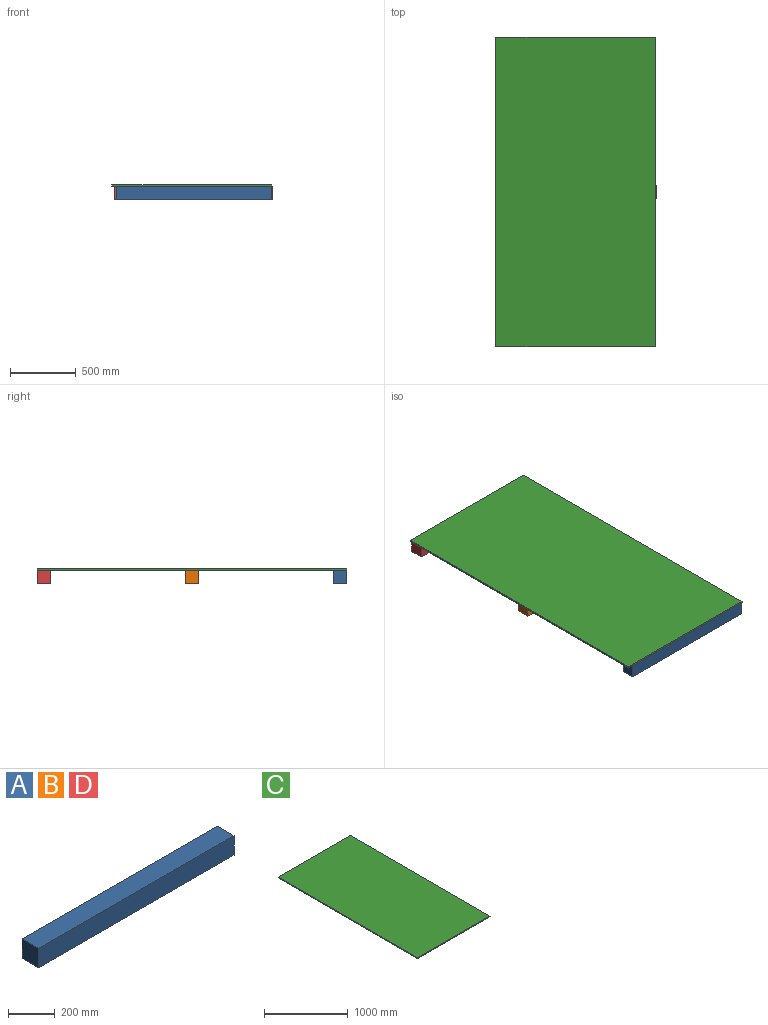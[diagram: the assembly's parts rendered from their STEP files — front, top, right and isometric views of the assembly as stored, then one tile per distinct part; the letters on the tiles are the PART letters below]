
ASSEMBLY  parts=4 mates=4
PART A: 6 faces, bbox 1181.1x101.6x101.6 mm
  f0: plane 1181.1x101.6mm, normal (0,-1,0), area 119999.8mm2, adj f1,f3,f4,f5
  f1: plane 1181.1x101.6mm, normal (0,0,-1), area 119999.8mm2, adj f0,f2,f4,f5
  f2: plane 1181.1x101.6mm, normal (0,1,0), area 119999.8mm2, adj f1,f3,f4,f5
  f3: plane 1181.1x101.6mm, normal (0,0,1), area 119999.8mm2, adj f0,f2,f4,f5
  f4: plane 101.6x101.6mm, normal (-1,0,0), area 10322.6mm2, adj f0,f1,f2,f3
  f5: plane 101.6x101.6mm, normal (1,0,0), area 10322.6mm2, adj f0,f1,f2,f3
PART B: same geometry as A
PART C: 6 faces, bbox 1219.2x2362.2x12.7 mm
  f0: plane 2362.2x12.7mm, normal (-1,0,0), area 29999.9mm2, adj f1,f3,f4,f5
  f1: plane 1219.2x12.7mm, normal (0,-1,0), area 15483.8mm2, adj f0,f2,f4,f5
  f2: plane 2362.2x12.7mm, normal (1,0,0), area 29999.9mm2, adj f1,f3,f4,f5
  f3: plane 1219.2x12.7mm, normal (0,1,0), area 15483.8mm2, adj f0,f2,f4,f5
  f4: plane 2362.2x1219.2mm, normal (0,0,1), area 2879994.2mm2, adj f0,f1,f2,f3
  f5: plane 2362.2x1219.2mm, normal (0,0,-1), area 2879994.2mm2, adj f0,f1,f2,f3
PART D: same geometry as A
PLACE A t=(-919.7,-1765.18,-465.86)mm
PLACE B t=(-916,-634.13,-465.86)mm
PLACE C t=(-938.75,-635.05,-415.06)mm
PLACE D t=(-938.21,495.61,-465.86)mm
MATE planar B.f3 <-> C.f5  axis (0,0,1) through (-916,-634.13,-415.06)mm
MATE planar D.f3 <-> C.f5  axis (0,0,1) through (-938.21,495.61,-415.06)mm
MATE planar A.f5 <-> C.f2  axis (1,0,0) through (-329.15,-1765.18,-465.86)mm
MATE planar C.f5 <-> A.f3  axis (0,0,-1) through (-938.75,-635.05,-415.06)mm
